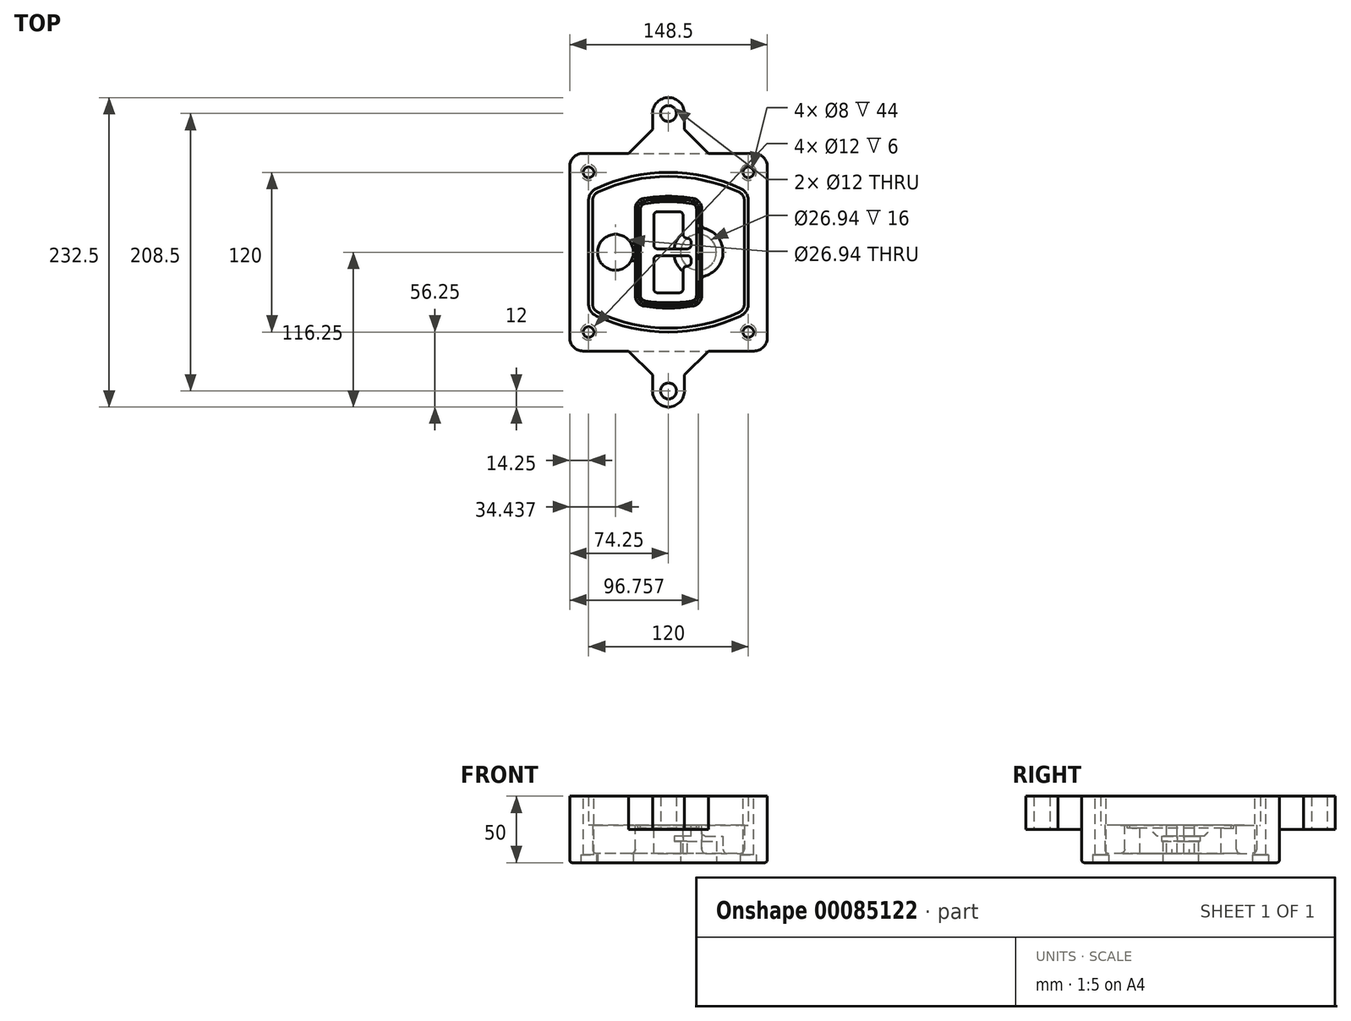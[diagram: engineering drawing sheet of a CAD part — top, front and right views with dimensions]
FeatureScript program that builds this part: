
annotation { "Feature Type Name" : "Feature", "Feature Type Description" : "" }
export const myFeature = defineFeature(function(context is Context, id is Id, definition is map)
    precondition{}
    {
        {
            var Q0;
            Q0=qCreatedBy(makeId("Top.planeOp"),FACE);
            var sketch = newSketch(context, id + "F0", { "sketchPlane" : qUnion([Q0])});
            skPoint(sketch, "E0.rect.middle", {"position": v(0, 0) * mm});
            skLineSegment(sketch, "E1.bottom", {"start": v(-64.25, -74.25) * mm, "end": v(64.25, -74.25) * mm});
            skLineSegment(sketch, "E1.top", {"start": v(-64.25, 74.25) * mm, "end": v(64.25, 74.25) * mm});
            skLineSegment(sketch, "E1.left", {"start": v(-74.25, -64.25) * mm, "end": v(-74.25, 64.25) * mm});
            skLineSegment(sketch, "E1.right", {"start": v(74.25, -64.25) * mm, "end": v(74.25, 64.25) * mm});
            skLineSegment(sketch, "E2", {"start": v(-74.25, 74.25) * mm, "end": v(74.25, -74.25) * mm, "construction": true});
            skLineSegment(sketch, "E3", {"start": v(74.25, 74.25) * mm, "end": v(-74.25, -74.25) * mm, "construction": true});
            skCircle(sketch, "E4", {"center": v(-60, 60) * mm, "radius": 4 * mm});
            skCircle(sketch, "E5", {"center": v(60, 60) * mm, "radius": 4 * mm});
            skCircle(sketch, "E6", {"center": v(60, -60) * mm, "radius": 4 * mm});
            skCircle(sketch, "E7", {"center": v(-60, -60) * mm, "radius": 4 * mm});
            skLineSegment(sketch, "E8", {"start": v(-60, 60) * mm, "end": v(60, 60) * mm, "construction": true});
            skLineSegment(sketch, "E9", {"start": v(60, 60) * mm, "end": v(60, -60) * mm, "construction": true});
            skLineSegment(sketch, "E10", {"start": v(60, -60) * mm, "end": v(-60, -60) * mm, "construction": true});
            skLineSegment(sketch, "E11", {"start": v(-60, -60) * mm, "end": v(-60, 60) * mm, "construction": true});
            skLineSegment(sketch, "E12", {"start": v(-60, 38.83) * mm, "end": v(-60, -38.83) * mm});
            skLineSegment(sketch, "E13", {"start": v(60, 38.83) * mm, "end": v(60, -38.83) * mm});
            skArc(sketch, "E14", {"start": v(54.26, 47.88) * mm, "mid": v(0, 60) * mm, "end": v(-54.26, 47.88) * mm});
            skArc(sketch, "E15", {"start": v(-54.26, -47.88) * mm, "mid": v(0, -60) * mm, "end": v(54.26, -47.88) * mm});
            skLineSegment(sketch, "E16", {"start": v(-60, 0) * mm, "end": v(60, 0) * mm, "construction": true});
            skPoint(sketch, "E17.visualSharp", {"position": v(-60, -45) * mm});
            skArc(sketch, "E17.filletArc", {"start": v(-60, -38.83) * mm, "mid": v(-58.44, -44.2) * mm, "end": v(-54.26, -47.88) * mm});
            skPoint(sketch, "E18.visualSharp", {"position": v(-60, 45) * mm});
            skArc(sketch, "E18.filletArc", {"start": v(-54.26, 47.88) * mm, "mid": v(-58.44, 44.2) * mm, "end": v(-60, 38.83) * mm});
            skPoint(sketch, "E19.visualSharp", {"position": v(60, 45) * mm});
            skArc(sketch, "E19.filletArc", {"start": v(60, 38.83) * mm, "mid": v(58.44, 44.2) * mm, "end": v(54.26, 47.88) * mm});
            skPoint(sketch, "E20.visualSharp", {"position": v(60, -45) * mm});
            skArc(sketch, "E20.filletArc", {"start": v(54.26, -47.88) * mm, "mid": v(58.44, -44.2) * mm, "end": v(60, -38.83) * mm});
            skPoint(sketch, "E21.visualSharp", {"position": v(-74.25, 74.25) * mm});
            skArc(sketch, "E21.filletArc", {"start": v(-64.25, 74.25) * mm, "mid": v(-71.32, 71.32) * mm, "end": v(-74.25, 64.25) * mm});
            skPoint(sketch, "E22.visualSharp", {"position": v(74.25, 74.25) * mm});
            skArc(sketch, "E22.filletArc", {"start": v(74.25, 64.25) * mm, "mid": v(71.32, 71.32) * mm, "end": v(64.25, 74.25) * mm});
            skPoint(sketch, "E23.visualSharp", {"position": v(74.25, -74.25) * mm});
            skArc(sketch, "E23.filletArc", {"start": v(64.25, -74.25) * mm, "mid": v(71.32, -71.32) * mm, "end": v(74.25, -64.25) * mm});
            skPoint(sketch, "E24.visualSharp", {"position": v(-74.25, -74.25) * mm});
            skArc(sketch, "E24.filletArc", {"start": v(-74.25, -64.25) * mm, "mid": v(-71.32, -71.32) * mm, "end": v(-64.25, -74.25) * mm});
            skArc(sketch, "E25.0", {"start": v(57, 38.83) * mm, "mid": v(55.9, 42.58) * mm, "end": v(52.98, 45.17) * mm});
            skLineSegment(sketch, "E25.1", {"start": v(57, 38.83) * mm, "end": v(57, -38.83) * mm});
            skArc(sketch, "E25.2", {"start": v(52.98, -45.17) * mm, "mid": v(55.9, -42.58) * mm, "end": v(57, -38.83) * mm});
            skArc(sketch, "E25.3", {"start": v(-52.98, -45.17) * mm, "mid": v(0, -57) * mm, "end": v(52.98, -45.17) * mm});
            skArc(sketch, "E25.4", {"start": v(-57, -38.83) * mm, "mid": v(-55.9, -42.58) * mm, "end": v(-52.98, -45.17) * mm});
            skArc(sketch, "E25.5", {"start": v(52.98, 45.17) * mm, "mid": v(0, 57) * mm, "end": v(-52.98, 45.17) * mm});
            skLineSegment(sketch, "E25.6", {"start": v(-57, 38.83) * mm, "end": v(-57, -38.83) * mm});
            skArc(sketch, "E25.7", {"start": v(-52.98, 45.17) * mm, "mid": v(-55.9, 42.58) * mm, "end": v(-57, 38.83) * mm});
            skArc(sketch, "E26.0", {"start": v(-55.96, 51.5) * mm, "mid": v(-61.82, 46.33) * mm, "end": v(-64, 38.83) * mm});
            skArc(sketch, "E26.1", {"start": v(55.96, 51.5) * mm, "mid": v(0, 64) * mm, "end": v(-55.96, 51.5) * mm});
            skArc(sketch, "E26.2", {"start": v(64, 38.83) * mm, "mid": v(61.82, 46.33) * mm, "end": v(55.96, 51.5) * mm});
            skLineSegment(sketch, "E26.3", {"start": v(64, 38.83) * mm, "end": v(64, -38.83) * mm});
            skArc(sketch, "E26.4", {"start": v(55.96, -51.5) * mm, "mid": v(61.82, -46.33) * mm, "end": v(64, -38.83) * mm});
            skLineSegment(sketch, "E26.5", {"start": v(-64, 38.83) * mm, "end": v(-64, -38.83) * mm});
            skArc(sketch, "E26.6", {"start": v(-55.96, -51.5) * mm, "mid": v(0, -64) * mm, "end": v(55.96, -51.5) * mm});
            skArc(sketch, "E26.7", {"start": v(-64, -38.83) * mm, "mid": v(-61.82, -46.33) * mm, "end": v(-55.96, -51.5) * mm});
            skSolve(sketch);
        }
        {
            var Q0;
            Q0=makeQuery(id+"F0.imprint","IMPRINT",FACE,{"disambiguationData":[TD([[makeQuery(id+"F0.imprint","IMPRINT",EDGE,{"derivedFrom":sQuery(id+"F0.wireOp",EDGE,"E1.bottom")}),1.0]])]});
            var Q1;
            Q1=makeQuery(id+"F0.imprint","IMPRINT",FACE,{"disambiguationData":[TD([[makeQuery(id+"F0.imprint","IMPRINT",EDGE,{"derivedFrom":sQuery(id+"F0.wireOp",EDGE,"E12")}),1.0]])]});
            var Q2;
            Q2=makeQuery(id+"F0.imprint","IMPRINT",FACE,{"disambiguationData":[TD([[makeQuery(id+"F0.imprint","IMPRINT",EDGE,{"derivedFrom":sQuery(id+"F0.wireOp",EDGE,"E25.0")}),1.0]])]});
            var Q3;
            Q3=makeQuery(id+"F0.imprint","IMPRINT",FACE,{"disambiguationData":[TD([[makeQuery(id+"F0.imprint","IMPRINT",EDGE,{"derivedFrom":sQuery(id+"F0.wireOp",EDGE,"E12")}),-1.0]])]});
            extrude(context, id + "F1", {"entities" : qUnion([Q0, Q1, Q2, Q3]), "oppositeDirection" : true, "depth" : 25 * mm});
        }
        {
            var Q0;
            Q0=makeQuery(id+"F0.imprint","IMPRINT",FACE,{"disambiguationData":[TD([[makeQuery(id+"F0.imprint","IMPRINT",EDGE,{"derivedFrom":sQuery(id+"F0.wireOp",EDGE,"E12")}),1.0]])]});
            extrude(context, id + "F2", {"entities" : qUnion([Q0]), "operationType" : NewBodyOperationType.ADD, "depth" : 3 * mm});
        }
        {
            var Q0;
            Q0=makeQuery(id+"F0.imprint","IMPRINT",FACE,{"disambiguationData":[TD([[makeQuery(id+"F0.imprint","IMPRINT",EDGE,{"derivedFrom":sQuery(id+"F0.wireOp",EDGE,"E25.0")}),1.0]])]});
            extrude(context, id + "F3", {"entities" : qUnion([Q0]), "operationType" : NewBodyOperationType.REMOVE, "oppositeDirection" : true, "depth" : 18 * mm});
        }
        {
            var Q0;
            Q0=makeQuery(id+"F2.opExtrude","CAP_FACE",FACE,{"disambiguationData":[OSD([sQuery(id+"F0.wireOp",EDGE,"E12"),sQuery(id+"F0.wireOp",EDGE,"E13"),sQuery(id+"F0.wireOp",EDGE,"E14"),sQuery(id+"F0.wireOp",EDGE,"E15"),sQuery(id+"F0.wireOp",EDGE,"E17.filletArc"),sQuery(id+"F0.wireOp",EDGE,"E18.filletArc"),sQuery(id+"F0.wireOp",EDGE,"E19.filletArc"),sQuery(id+"F0.wireOp",EDGE,"E20.filletArc"),sQuery(id+"F0.wireOp",EDGE,"E25.0"),sQuery(id+"F0.wireOp",EDGE,"E25.1"),sQuery(id+"F0.wireOp",EDGE,"E25.2"),sQuery(id+"F0.wireOp",EDGE,"E25.3"),sQuery(id+"F0.wireOp",EDGE,"E25.4"),sQuery(id+"F0.wireOp",EDGE,"E25.5"),sQuery(id+"F0.wireOp",EDGE,"E25.6"),sQuery(id+"F0.wireOp",EDGE,"E25.7")])],"isStart":false});
            var sketch = newSketch(context, id + "F4", { "sketchPlane" : qUnion([Q0])});
            skArc(sketch, "E27.0", {"start": v(-18.34, -40.45) * mm, "mid": v(0, -42) * mm, "end": v(18.34, -40.45) * mm});
            skArc(sketch, "E28.0", {"start": v(18.34, 40.45) * mm, "mid": v(0, 42) * mm, "end": v(-18.34, 40.45) * mm});
            skLineSegment(sketch, "E29", {"start": v(-25, 32.57) * mm, "end": v(-25, -32.57) * mm});
            skLineSegment(sketch, "E30", {"start": v(25, 32.57) * mm, "end": v(25, -32.57) * mm});
            skLineSegment(sketch, "E31", {"start": v(-25, 39.1) * mm, "end": v(25, 39.1) * mm, "construction": true});
            skLineSegment(sketch, "E32", {"start": v(-25, -39.1) * mm, "end": v(25, -39.1) * mm, "construction": true});
            skPoint(sketch, "E33.visualSharp", {"position": v(-25, 39.1) * mm});
            skArc(sketch, "E33.filletArc", {"start": v(-18.34, 40.45) * mm, "mid": v(-23.11, 37.73) * mm, "end": v(-25, 32.57) * mm});
            skPoint(sketch, "E34.visualSharp", {"position": v(25, 39.1) * mm});
            skArc(sketch, "E34.filletArc", {"start": v(25, 32.57) * mm, "mid": v(23.11, 37.73) * mm, "end": v(18.34, 40.45) * mm});
            skPoint(sketch, "E35.visualSharp", {"position": v(25, -39.1) * mm});
            skArc(sketch, "E35.filletArc", {"start": v(18.34, -40.45) * mm, "mid": v(23.11, -37.73) * mm, "end": v(25, -32.57) * mm});
            skPoint(sketch, "E36.visualSharp", {"position": v(-25, -39.1) * mm});
            skArc(sketch, "E36.filletArc", {"start": v(-25, -32.57) * mm, "mid": v(-23.11, -37.73) * mm, "end": v(-18.34, -40.45) * mm});
            skArc(sketch, "E37.0", {"start": v(52.98, 45.17) * mm, "mid": v(0, 57) * mm, "end": v(-52.98, 45.17) * mm});
            skArc(sketch, "E37.1", {"start": v(-52.98, 45.17) * mm, "mid": v(-55.9, 42.58) * mm, "end": v(-57, 38.83) * mm});
            skLineSegment(sketch, "E37.2", {"start": v(-57, 38.83) * mm, "end": v(-57, -38.83) * mm});
            skArc(sketch, "E37.3", {"start": v(-57, -38.83) * mm, "mid": v(-55.9, -42.58) * mm, "end": v(-52.98, -45.17) * mm});
            skArc(sketch, "E37.4", {"start": v(-52.98, -45.17) * mm, "mid": v(0, -57) * mm, "end": v(52.98, -45.17) * mm});
            skArc(sketch, "E37.5", {"start": v(52.98, -45.17) * mm, "mid": v(55.9, -42.58) * mm, "end": v(57, -38.83) * mm});
            skLineSegment(sketch, "E37.6", {"start": v(57, 38.83) * mm, "end": v(57, -38.83) * mm});
            skArc(sketch, "E37.7", {"start": v(57, 38.83) * mm, "mid": v(55.9, 42.58) * mm, "end": v(52.98, 45.17) * mm});
            skLineSegment(sketch, "E38.0", {"start": v(23, 32.57) * mm, "end": v(23, -32.57) * mm});
            skArc(sketch, "E38.1", {"start": v(18, -38.48) * mm, "mid": v(21.58, -36.44) * mm, "end": v(23, -32.57) * mm});
            skArc(sketch, "E38.2", {"start": v(-18, -38.48) * mm, "mid": v(0, -40) * mm, "end": v(18, -38.48) * mm});
            skArc(sketch, "E38.3", {"start": v(-23, -32.57) * mm, "mid": v(-21.58, -36.44) * mm, "end": v(-18, -38.48) * mm});
            skLineSegment(sketch, "E38.4", {"start": v(-23, 32.57) * mm, "end": v(-23, -32.57) * mm});
            skArc(sketch, "E38.5", {"start": v(23, 32.57) * mm, "mid": v(21.58, 36.44) * mm, "end": v(18, 38.48) * mm});
            skArc(sketch, "E38.6", {"start": v(-18, 38.48) * mm, "mid": v(-21.58, 36.44) * mm, "end": v(-23, 32.57) * mm});
            skArc(sketch, "E38.7", {"start": v(18, 38.48) * mm, "mid": v(0, 40) * mm, "end": v(-18, 38.48) * mm});
            skArc(sketch, "E39.0", {"start": v(21, 32.57) * mm, "mid": v(20.06, 35.15) * mm, "end": v(17.67, 36.5) * mm});
            skLineSegment(sketch, "E39.1", {"start": v(21, 32.57) * mm, "end": v(21, -32.57) * mm});
            skArc(sketch, "E39.2", {"start": v(17.67, -36.5) * mm, "mid": v(20.06, -35.15) * mm, "end": v(21, -32.57) * mm});
            skArc(sketch, "E39.3", {"start": v(-17.67, -36.5) * mm, "mid": v(0, -38) * mm, "end": v(17.67, -36.5) * mm});
            skArc(sketch, "E39.4", {"start": v(-21, -32.57) * mm, "mid": v(-20.06, -35.15) * mm, "end": v(-17.67, -36.5) * mm});
            skArc(sketch, "E39.5", {"start": v(17.67, 36.5) * mm, "mid": v(0, 38) * mm, "end": v(-17.67, 36.5) * mm});
            skLineSegment(sketch, "E39.6", {"start": v(-21, 32.57) * mm, "end": v(-21, -32.57) * mm});
            skArc(sketch, "E39.7", {"start": v(-17.67, 36.5) * mm, "mid": v(-20.06, 35.15) * mm, "end": v(-21, 32.57) * mm});
            skLineSegment(sketch, "E40", {"start": v(-25, 0) * mm, "end": v(25, 0) * mm, "construction": true});
            skLineSegment(sketch, "E41", {"start": v(-11, 5.5) * mm, "end": v(-11, 27.5) * mm});
            skLineSegment(sketch, "E42", {"start": v(-8, 30.5) * mm, "end": v(8, 30.5) * mm});
            skLineSegment(sketch, "E43", {"start": v(11, 27.5) * mm, "end": v(11, 13.5) * mm});
            skLineSegment(sketch, "E44", {"start": v(14, 10.5) * mm, "end": v(14, 10.5) * mm});
            skLineSegment(sketch, "E45", {"start": v(17, 7.5) * mm, "end": v(17, 5.5) * mm});
            skLineSegment(sketch, "E46", {"start": v(14, 2.5) * mm, "end": v(-8, 2.5) * mm});
            skPoint(sketch, "E47.visualSharp", {"position": v(-11, 30.5) * mm});
            skArc(sketch, "E47.filletArc", {"start": v(-8, 30.5) * mm, "mid": v(-10.12, 29.62) * mm, "end": v(-11, 27.5) * mm});
            skPoint(sketch, "E48.visualSharp", {"position": v(11, 30.5) * mm});
            skArc(sketch, "E48.filletArc", {"start": v(11, 27.5) * mm, "mid": v(10.12, 29.62) * mm, "end": v(8, 30.5) * mm});
            skPoint(sketch, "E49.visualSharp", {"position": v(11, 10.5) * mm});
            skArc(sketch, "E49.filletArc", {"start": v(11, 13.5) * mm, "mid": v(11.88, 11.38) * mm, "end": v(14, 10.5) * mm});
            skPoint(sketch, "E50.visualSharp", {"position": v(17, 10.5) * mm});
            skArc(sketch, "E50.filletArc", {"start": v(17, 7.5) * mm, "mid": v(16.12, 9.62) * mm, "end": v(14, 10.5) * mm});
            skPoint(sketch, "E51.visualSharp", {"position": v(17, 2.5) * mm});
            skArc(sketch, "E51.filletArc", {"start": v(14, 2.5) * mm, "mid": v(16.12, 3.38) * mm, "end": v(17, 5.5) * mm});
            skPoint(sketch, "E52.visualSharp", {"position": v(-11, 2.5) * mm});
            skArc(sketch, "E52.filletArc", {"start": v(-11, 5.5) * mm, "mid": v(-10.12, 3.38) * mm, "end": v(-8, 2.5) * mm});
            skLineSegment(sketch, "E53.0.MirrorCS", {"start": v(14, -2.5) * mm, "end": v(-8, -2.5) * mm});
            skArc(sketch, "E54.0.MirrorCS", {"start": v(-11, -5.5) * mm, "mid": v(-10.12, -3.38) * mm, "end": v(-8, -2.5) * mm});
            skLineSegment(sketch, "E55.0.MirrorCS", {"start": v(-11, -5.5) * mm, "end": v(-11, -27.5) * mm});
            skArc(sketch, "E56.0.MirrorCS", {"start": v(-8, -30.5) * mm, "mid": v(-10.12, -29.62) * mm, "end": v(-11, -27.5) * mm});
            skLineSegment(sketch, "E57.0.MirrorCS", {"start": v(-8, -30.5) * mm, "end": v(8, -30.5) * mm});
            skArc(sketch, "E58.0.MirrorCS", {"start": v(11, -27.5) * mm, "mid": v(10.12, -29.62) * mm, "end": v(8, -30.5) * mm});
            skLineSegment(sketch, "E59.0.MirrorCS", {"start": v(11, -27.5) * mm, "end": v(11, -13.5) * mm});
            skArc(sketch, "E60.0.MirrorCS", {"start": v(11, -13.5) * mm, "mid": v(11.88, -11.38) * mm, "end": v(14, -10.5) * mm});
            skArc(sketch, "E61.0.MirrorCS", {"start": v(17, -7.5) * mm, "mid": v(16.12, -9.62) * mm, "end": v(14, -10.5) * mm});
            skLineSegment(sketch, "E62.0.MirrorCS", {"start": v(17, -7.5) * mm, "end": v(17, -5.5) * mm});
            skArc(sketch, "E63.0.MirrorCS", {"start": v(14, -2.5) * mm, "mid": v(16.12, -3.38) * mm, "end": v(17, -5.5) * mm});
            skSolve(sketch);
        }
        {
            var Q0;
            Q0=makeQuery(id+"F4.imprint","IMPRINT",FACE,{"disambiguationData":[TD([[makeQuery(id+"F4.imprint","IMPRINT",EDGE,{"derivedFrom":sQuery(id+"F4.wireOp",EDGE,"E27.0")}),1.0]])]});
            var Q1;
            Q1=makeQuery(id+"F4.imprint","IMPRINT",FACE,{"disambiguationData":[TD([[makeQuery(id+"F4.imprint","IMPRINT",EDGE,{"derivedFrom":sQuery(id+"F4.wireOp",EDGE,"E38.0")}),-1.0]])]});
            var Q2;
            Q2=makeQuery(id+"F4.imprint","IMPRINT",FACE,{"disambiguationData":[TD([[makeQuery(id+"F4.imprint","IMPRINT",EDGE,{"derivedFrom":sQuery(id+"F4.wireOp",EDGE,"E39.0")}),1.0]])]});
            extrude(context, id + "F5", {"entities" : qUnion([Q0, Q1, Q2]), "operationType" : NewBodyOperationType.ADD, "endBound" : BoundingType.UP_TO_NEXT, "oppositeDirection" : true, "depth" : 25 * mm});
        }
        {
            var Q0;
            Q0=makeQuery(id+"F4.imprint","IMPRINT",FACE,{"disambiguationData":[TD([[makeQuery(id+"F4.imprint","IMPRINT",EDGE,{"derivedFrom":sQuery(id+"F4.wireOp",EDGE,"E38.0")}),-1.0]])]});
            extrude(context, id + "F6", {"entities" : qUnion([Q0]), "operationType" : NewBodyOperationType.REMOVE, "oppositeDirection" : true, "depth" : 2 * mm});
        }
        {
            var Q0;
            Q0=makeQuery(id+"F1.opExtrude","CAP_FACE",FACE,{"disambiguationData":[OSD([sQuery(id+"F0.wireOp",EDGE,"E1.bottom"),sQuery(id+"F0.wireOp",EDGE,"E1.top"),sQuery(id+"F0.wireOp",EDGE,"E1.left"),sQuery(id+"F0.wireOp",EDGE,"E1.right"),sQuery(id+"F0.wireOp",EDGE,"E4"),sQuery(id+"F0.wireOp",EDGE,"E5"),sQuery(id+"F0.wireOp",EDGE,"E6"),sQuery(id+"F0.wireOp",EDGE,"E7"),sQuery(id+"F0.wireOp",EDGE,"E21.filletArc"),sQuery(id+"F0.wireOp",EDGE,"E22.filletArc"),sQuery(id+"F0.wireOp",EDGE,"E23.filletArc"),sQuery(id+"F0.wireOp",EDGE,"E24.filletArc")])],"isStart":false});
            var sketch = newSketch(context, id + "F7", { "sketchPlane" : qUnion([Q0])});
            skCircle(sketch, "E64", {"center": v(22.5, 0) * mm, "radius": 13.47 * mm});
            skCircle(sketch, "E65", {"center": v(-39.81, 0) * mm, "radius": 13.47 * mm});
            skLineSegment(sketch, "E66", {"start": v(74.25, 0) * mm, "end": v(-74.25, 0) * mm});
            skCircle(sketch, "E67", {"center": v(22.5, 0) * mm, "radius": 18.47 * mm});
            skCircle(sketch, "E68", {"center": v(60, -60) * mm, "radius": 6 * mm});
            skCircle(sketch, "E69", {"center": v(-60, -60) * mm, "radius": 6 * mm});
            skCircle(sketch, "E70", {"center": v(-60, 60) * mm, "radius": 6 * mm});
            skCircle(sketch, "E71", {"center": v(60, 60) * mm, "radius": 6 * mm});
            skSolve(sketch);
        }
        {
            var Q0;
            {var subQ1=sQuery(id+"F7.wireOp",EDGE,"E66");var subQ4=sQuery(id+"F7.wireOp",EDGE,"E64");var subQ6=makeQuery(id+"F7.imprint","INTERSECT",VERTEX,{"disambiguationData":[OD(0.0)],"derivedFrom":[subQ4,subQ1]});Q0=makeQuery(id+"F7.imprint","IMPRINT",FACE,{"disambiguationData":[TD([[makeQuery(id+"F7.imprint","IMPRINT",EDGE,{"disambiguationData":[TD([[subQ6,-1.0]])],"derivedFrom":subQ4}),-1.0]])]});}
            var Q1;
            {var subQ0=sQuery(id+"F7.wireOp",EDGE,"E66");var subQ1=sQuery(id+"F7.wireOp",EDGE,"E64");var subQ3=makeQuery(id+"F7.imprint","INTERSECT",VERTEX,{"disambiguationData":[OD(0.0)],"derivedFrom":[subQ1,subQ0]});Q1=makeQuery(id+"F7.imprint","IMPRINT",FACE,{"disambiguationData":[TD([[makeQuery(id+"F7.imprint","IMPRINT",EDGE,{"disambiguationData":[TD([[subQ3,-1.0]])],"derivedFrom":subQ1}),1.0]])]});}
            var Q2;
            {var subQ0=sQuery(id+"F7.wireOp",EDGE,"E66");var subQ1=sQuery(id+"F7.wireOp",EDGE,"E64");var subQ3=makeQuery(id+"F7.imprint","INTERSECT",VERTEX,{"disambiguationData":[OD(0.0)],"derivedFrom":[subQ1,subQ0]});Q2=makeQuery(id+"F7.imprint","IMPRINT",FACE,{"disambiguationData":[TD([[makeQuery(id+"F7.imprint","IMPRINT",EDGE,{"disambiguationData":[TD([[subQ3,1.0]])],"derivedFrom":subQ1}),1.0]])]});}
            var Q3;
            {var subQ1=sQuery(id+"F7.wireOp",EDGE,"E66");var subQ4=sQuery(id+"F7.wireOp",EDGE,"E64");var subQ6=makeQuery(id+"F7.imprint","INTERSECT",VERTEX,{"disambiguationData":[OD(0.0)],"derivedFrom":[subQ4,subQ1]});Q3=makeQuery(id+"F7.imprint","IMPRINT",FACE,{"disambiguationData":[TD([[makeQuery(id+"F7.imprint","IMPRINT",EDGE,{"disambiguationData":[TD([[subQ6,1.0]])],"derivedFrom":subQ4}),-1.0]])]});}
            extrude(context, id + "F8", {"entities" : qUnion([Q0, Q1, Q2, Q3]), "operationType" : NewBodyOperationType.ADD, "oppositeDirection" : true, "depth" : 20 * mm});
        }
        {
            var Q0;
            {var subQ0=sQuery(id+"F7.wireOp",EDGE,"E66");var subQ1=sQuery(id+"F7.wireOp",EDGE,"E64");var subQ3=makeQuery(id+"F7.imprint","INTERSECT",VERTEX,{"disambiguationData":[OD(0.0)],"derivedFrom":[subQ1,subQ0]});Q0=makeQuery(id+"F7.imprint","IMPRINT",FACE,{"disambiguationData":[TD([[makeQuery(id+"F7.imprint","IMPRINT",EDGE,{"disambiguationData":[TD([[subQ3,-1.0]])],"derivedFrom":subQ1}),1.0]])]});}
            var Q1;
            {var subQ0=sQuery(id+"F7.wireOp",EDGE,"E66");var subQ1=sQuery(id+"F7.wireOp",EDGE,"E64");var subQ3=makeQuery(id+"F7.imprint","INTERSECT",VERTEX,{"disambiguationData":[OD(0.0)],"derivedFrom":[subQ1,subQ0]});Q1=makeQuery(id+"F7.imprint","IMPRINT",FACE,{"disambiguationData":[TD([[makeQuery(id+"F7.imprint","IMPRINT",EDGE,{"disambiguationData":[TD([[subQ3,1.0]])],"derivedFrom":subQ1}),1.0]])]});}
            extrude(context, id + "F9", {"entities" : qUnion([Q0, Q1]), "operationType" : NewBodyOperationType.REMOVE, "oppositeDirection" : true, "depth" : 16 * mm});
        }
        {
            var Q0;
            {var subQ0=sQuery(id+"F7.wireOp",EDGE,"E66");var subQ1=sQuery(id+"F7.wireOp",EDGE,"E65");var subQ3=makeQuery(id+"F7.imprint","INTERSECT",VERTEX,{"disambiguationData":[OD(0.0)],"derivedFrom":[subQ1,subQ0]});Q0=makeQuery(id+"F7.imprint","IMPRINT",FACE,{"disambiguationData":[TD([[makeQuery(id+"F7.imprint","IMPRINT",EDGE,{"disambiguationData":[TD([[subQ3,-1.0]])],"derivedFrom":subQ1}),1.0]])]});}
            var Q1;
            {var subQ0=sQuery(id+"F7.wireOp",EDGE,"E66");var subQ1=sQuery(id+"F7.wireOp",EDGE,"E65");var subQ3=makeQuery(id+"F7.imprint","INTERSECT",VERTEX,{"disambiguationData":[OD(0.0)],"derivedFrom":[subQ1,subQ0]});Q1=makeQuery(id+"F7.imprint","IMPRINT",FACE,{"disambiguationData":[TD([[makeQuery(id+"F7.imprint","IMPRINT",EDGE,{"disambiguationData":[TD([[subQ3,1.0]])],"derivedFrom":subQ1}),1.0]])]});}
            extrude(context, id + "F10", {"entities" : qUnion([Q0, Q1]), "operationType" : NewBodyOperationType.REMOVE, "oppositeDirection" : true, "depth" : 25 * mm});
        }
        {
            var Q0;
            Q0=makeQuery(id+"F7.imprint","IMPRINT",FACE,{"disambiguationData":[TD([[makeQuery(id+"F7.imprint","IMPRINT",EDGE,{"derivedFrom":sQuery(id+"F7.wireOp",EDGE,"E68")}),1.0]])]});
            var Q1;
            Q1=makeQuery(id+"F7.imprint","IMPRINT",FACE,{"disambiguationData":[TD([[makeQuery(id+"F7.imprint","IMPRINT",EDGE,{"derivedFrom":makeQuery(id+"F1.opExtrude","CAP_EDGE",EDGE,{"disambiguationData":[OSD([sQuery(id+"F0.wireOp",EDGE,"E5")])],"isStart":false})}),-1.0]])]});
            var Q2;
            Q2=makeQuery(id+"F7.imprint","IMPRINT",FACE,{"disambiguationData":[TD([[makeQuery(id+"F7.imprint","IMPRINT",EDGE,{"derivedFrom":sQuery(id+"F7.wireOp",EDGE,"E69")}),1.0]])]});
            var Q3;
            Q3=makeQuery(id+"F7.imprint","IMPRINT",FACE,{"disambiguationData":[TD([[makeQuery(id+"F7.imprint","IMPRINT",EDGE,{"derivedFrom":makeQuery(id+"F1.opExtrude","CAP_EDGE",EDGE,{"disambiguationData":[OSD([sQuery(id+"F0.wireOp",EDGE,"E4")])],"isStart":false})}),-1.0]])]});
            var Q4;
            Q4=makeQuery(id+"F7.imprint","IMPRINT",FACE,{"disambiguationData":[TD([[makeQuery(id+"F7.imprint","IMPRINT",EDGE,{"derivedFrom":sQuery(id+"F7.wireOp",EDGE,"E70")}),1.0]])]});
            var Q5;
            Q5=makeQuery(id+"F7.imprint","IMPRINT",FACE,{"disambiguationData":[TD([[makeQuery(id+"F7.imprint","IMPRINT",EDGE,{"derivedFrom":makeQuery(id+"F1.opExtrude","CAP_EDGE",EDGE,{"disambiguationData":[OSD([sQuery(id+"F0.wireOp",EDGE,"E7")])],"isStart":false})}),-1.0]])]});
            var Q6;
            Q6=makeQuery(id+"F7.imprint","IMPRINT",FACE,{"disambiguationData":[TD([[makeQuery(id+"F7.imprint","IMPRINT",EDGE,{"derivedFrom":sQuery(id+"F7.wireOp",EDGE,"E71")}),1.0]])]});
            var Q7;
            Q7=makeQuery(id+"F7.imprint","IMPRINT",FACE,{"disambiguationData":[TD([[makeQuery(id+"F7.imprint","IMPRINT",EDGE,{"derivedFrom":makeQuery(id+"F1.opExtrude","CAP_EDGE",EDGE,{"disambiguationData":[OSD([sQuery(id+"F0.wireOp",EDGE,"E6")])],"isStart":false})}),-1.0]])]});
            extrude(context, id + "F11", {"entities" : qUnion([Q0, Q1, Q2, Q3, Q4, Q5, Q6, Q7]), "operationType" : NewBodyOperationType.REMOVE, "oppositeDirection" : true, "depth" : 6 * mm});
        }
        {
            var Q0;
            Q0=makeQuery(id+"F9.boolean.opBoolean","COPY",FACE,{"derivedFrom":makeQuery(id+"F9.opExtrude","CAP_FACE",FACE,{"disambiguationData":[OSD([sQuery(id+"F7.wireOp",EDGE,"E64")])],"isStart":false})});
            var sketch = newSketch(context, id + "F12", { "sketchPlane" : qUnion([Q0])});
            skArc(sketch, "E72.0", {"start": v(11, 14.45) * mm, "mid": v(6.45, 9.13) * mm, "end": v(4.2, 2.5) * mm});
            skArc(sketch, "E72.1", {"start": v(4.2, -2.5) * mm, "mid": v(6.45, -9.13) * mm, "end": v(11, -14.45) * mm});
            skLineSegment(sketch, "E73", {"start": v(4.2, -2.5) * mm, "end": v(14, -2.5) * mm});
            skLineSegment(sketch, "E74.0", {"start": v(14, 2.5) * mm, "end": v(4.2, 2.5) * mm});
            skArc(sketch, "E74.1", {"start": v(14, 2.5) * mm, "mid": v(16.12, 3.38) * mm, "end": v(17, 5.5) * mm});
            skLineSegment(sketch, "E74.2", {"start": v(17, 7.5) * mm, "end": v(17, 5.5) * mm});
            skArc(sketch, "E74.3", {"start": v(17, 7.5) * mm, "mid": v(16.12, 9.62) * mm, "end": v(14, 10.5) * mm});
            skArc(sketch, "E74.4", {"start": v(11, 13.5) * mm, "mid": v(11.88, 11.38) * mm, "end": v(14, 10.5) * mm});
            skLineSegment(sketch, "E74.5", {"start": v(11, 14.45) * mm, "end": v(11, 13.5) * mm});
            skLineSegment(sketch, "E74.7", {"start": v(14, -2.5) * mm, "end": v(4.2, -2.5) * mm});
            skArc(sketch, "E74.8", {"start": v(14, -2.5) * mm, "mid": v(16.12, -3.38) * mm, "end": v(17, -5.5) * mm});
            skLineSegment(sketch, "E74.9", {"start": v(17, -7.5) * mm, "end": v(17, -5.5) * mm});
            skArc(sketch, "E74.10", {"start": v(17, -7.5) * mm, "mid": v(16.12, -9.62) * mm, "end": v(14, -10.5) * mm});
            skArc(sketch, "E74.11", {"start": v(11, -13.5) * mm, "mid": v(11.88, -11.38) * mm, "end": v(14, -10.5) * mm});
            skLineSegment(sketch, "E74.12", {"start": v(11, -14.45) * mm, "end": v(11, -13.5) * mm});
            skPoint(sketch, "E75.orphan", {"position": v(11, -27.5) * mm});
            skPoint(sketch, "E76.orphan", {"position": v(-8, -2.5) * mm});
            skPoint(sketch, "E77.orphan", {"position": v(-8, 2.5) * mm});
            skPoint(sketch, "E78.orphan", {"position": v(11, 27.5) * mm});
            skSolve(sketch);
        }
        {
            var Q0;
            {var subQ7=sQuery(id+"F12.wireOp",EDGE,"E72.0");var subQ14=sQuery(id+"F12.wireOp",EDGE,"E72.1");var subQ16=sQuery(id+"F12.wireOp",EDGE,"E74.1");var subQ18=sQuery(id+"F12.wireOp",EDGE,"E74.8");Q0=qUnion([makeQuery(id+"F12.imprint","IMPRINT",FACE,{"disambiguationData":[TD([[makeQuery(id+"F12.imprint","IMPRINT",EDGE,{"derivedFrom":subQ7}),1.0]])]}),makeQuery(id+"F12.imprint","IMPRINT",FACE,{"disambiguationData":[TD([[makeQuery(id+"F12.imprint","IMPRINT",EDGE,{"derivedFrom":subQ14}),1.0]])]}),makeQuery(id+"F12.imprint","IMPRINT",FACE,{"disambiguationData":[TD([[makeQuery(id+"F12.imprint","IMPRINT",EDGE,{"derivedFrom":subQ16}),1.0]])]}),makeQuery(id+"F12.imprint","IMPRINT",FACE,{"disambiguationData":[TD([[makeQuery(id+"F12.imprint","IMPRINT",EDGE,{"derivedFrom":subQ18}),-1.0]])]})]);}
            var Q1;
            Q1=makeQuery(id+"F5.boolean.opBoolean","SPLIT",FACE,{"disambiguationData":[TD([makeQuery(id+"F5.opExtrude","SWEPT_FACE",FACE,{"disambiguationData":[OSD([sQuery(id+"F4.wireOp",EDGE,"E41")])]})])],"derivedFrom":makeQuery(id+"F3.boolean.opBoolean","COPY",FACE,{"derivedFrom":makeQuery(id+"F3.opExtrude","CAP_FACE",FACE,{"disambiguationData":[OSD([sQuery(id+"F0.wireOp",EDGE,"E25.0"),sQuery(id+"F0.wireOp",EDGE,"E25.1"),sQuery(id+"F0.wireOp",EDGE,"E25.2"),sQuery(id+"F0.wireOp",EDGE,"E25.3"),sQuery(id+"F0.wireOp",EDGE,"E25.4"),sQuery(id+"F0.wireOp",EDGE,"E25.5"),sQuery(id+"F0.wireOp",EDGE,"E25.6"),sQuery(id+"F0.wireOp",EDGE,"E25.7")])],"isStart":false})})});
            extrude(context, id + "F13", {"entities" : qUnion([Q0]), "operationType" : NewBodyOperationType.REMOVE, "endBound" : BoundingType.UP_TO_SURFACE, "endBoundEntityFace" : qUnion([Q1]), "depth" : 25 * mm});
        }
        {
            var Q0;
            Q0=makeQuery(id+"F3.boolean.opBoolean","COPY",EDGE,{"derivedFrom":makeQuery(id+"F3.opExtrude","CAP_EDGE",EDGE,{"disambiguationData":[OSD([sQuery(id+"F0.wireOp",EDGE,"E25.6")])],"isStart":false})});
            var Q1;
            Q1=makeQuery(id+"F8.boolean.opBoolean","INTERSECT",EDGE,{"derivedFrom":[makeQuery(id+"F5.opExtrude","SWEPT_FACE",FACE,{"disambiguationData":[OSD([sQuery(id+"F4.wireOp",EDGE,"E30")])]}),makeQuery(id+"F8.opExtrude","CAP_FACE",FACE,{"disambiguationData":[OSD([sQuery(id+"F7.wireOp",EDGE,"E67")])],"isStart":false})]});
            var Q2;
            Q2=makeQuery(id+"F8.boolean.opBoolean","INTERSECT",EDGE,{"disambiguationData":[OD(1.0)],"derivedFrom":[makeQuery(id+"F5.opExtrude","SWEPT_FACE",FACE,{"disambiguationData":[OSD([sQuery(id+"F4.wireOp",EDGE,"E30")])]}),makeQuery(id+"F8.opExtrude","SWEPT_FACE",FACE,{"disambiguationData":[OSD([sQuery(id+"F7.wireOp",EDGE,"E67")])]})]});
            var Q3;
            {var subQ0=sQuery(id+"F4.wireOp",EDGE,"E30");Q3=makeQuery(id+"F8.boolean.opBoolean","SPLIT",EDGE,{"disambiguationData":[TD([makeQuery(id+"F5.opExtrude","SWEPT_FACE",FACE,{"disambiguationData":[OSD([sQuery(id+"F4.wireOp",EDGE,"E35.filletArc")])]})])],"derivedFrom":makeQuery(id+"F5.opExtrude","CAP_EDGE",EDGE,{"disambiguationData":[OSD([subQ0])],"isStart":false})});}
            var Q4;
            {var subQ0=sQuery(id+"F0.wireOp",EDGE,"E25.7");var subQ1=sQuery(id+"F0.wireOp",EDGE,"E25.1");var subQ2=sQuery(id+"F0.wireOp",EDGE,"E25.6");var subQ3=sQuery(id+"F0.wireOp",EDGE,"E25.5");var subQ4=sQuery(id+"F0.wireOp",EDGE,"E25.4");var subQ5=sQuery(id+"F0.wireOp",EDGE,"E25.0");var subQ6=sQuery(id+"F0.wireOp",EDGE,"E25.2");var subQ7=sQuery(id+"F0.wireOp",EDGE,"E25.3");Q4=makeQuery(id+"F8.boolean.opBoolean","INTERSECT",EDGE,{"derivedFrom":[makeQuery(id+"F5.boolean.opBoolean","SPLIT",FACE,{"disambiguationData":[TD([makeQuery(id+"F2.opExtrude","SWEPT_FACE",FACE,{"disambiguationData":[OSD([subQ5])]})])],"derivedFrom":makeQuery(id+"F3.boolean.opBoolean","COPY",FACE,{"derivedFrom":makeQuery(id+"F3.opExtrude","CAP_FACE",FACE,{"disambiguationData":[OSD([subQ5,subQ1,subQ6,subQ7,subQ4,subQ3,subQ2,subQ0])],"isStart":false})})}),makeQuery(id+"F8.opExtrude","SWEPT_FACE",FACE,{"disambiguationData":[OSD([sQuery(id+"F7.wireOp",EDGE,"E67")])]})]});}
            var Q5;
            Q5=makeQuery(id+"F8.boolean.opBoolean","INTERSECT",EDGE,{"disambiguationData":[OD(0.0)],"derivedFrom":[makeQuery(id+"F5.opExtrude","SWEPT_FACE",FACE,{"disambiguationData":[OSD([sQuery(id+"F4.wireOp",EDGE,"E30")])]}),makeQuery(id+"F8.opExtrude","SWEPT_FACE",FACE,{"disambiguationData":[OSD([sQuery(id+"F7.wireOp",EDGE,"E67")])]})]});
            fillet(context, id + "F14", {"entities" : qUnion([Q0, Q1, Q2, Q3, Q4, Q5]), "radius" : 3 * mm, "tangentPropagation" : true, "allowEdgeOverflow" : false});
        }
        {
            var Q0;
            Q0=makeQuery(id+"F1.opExtrude","CAP_EDGE",EDGE,{"disambiguationData":[OSD([sQuery(id+"F0.wireOp",EDGE,"E1.bottom")])],"isStart":false});
            fillet(context, id + "F15", {"entities" : qUnion([Q0]), "radius" : 2 * mm, "tangentPropagation" : true, "allowEdgeOverflow" : false});
        }
        {
            var Q0;
            {var subQ0=sQuery(id+"F0.wireOp",EDGE,"E22.filletArc");var subQ1=sQuery(id+"F0.wireOp",EDGE,"E7");var subQ2=sQuery(id+"F0.wireOp",EDGE,"E6");var subQ3=sQuery(id+"F0.wireOp",EDGE,"E5");var subQ4=sQuery(id+"F0.wireOp",EDGE,"E4");var subQ5=sQuery(id+"F0.wireOp",EDGE,"E1.bottom");var subQ6=sQuery(id+"F0.wireOp",EDGE,"E21.filletArc");var subQ7=sQuery(id+"F0.wireOp",EDGE,"E1.top");var subQ8=sQuery(id+"F0.wireOp",EDGE,"E1.left");var subQ9=sQuery(id+"F0.wireOp",EDGE,"E1.right");var subQ10=sQuery(id+"F0.wireOp",EDGE,"E23.filletArc");var subQ11=sQuery(id+"F0.wireOp",EDGE,"E24.filletArc");Q0=makeQuery(id+"F2.boolean.opBoolean","SPLIT",FACE,{"disambiguationData":[TD([makeQuery(id+"F1.opExtrude","SWEPT_FACE",FACE,{"disambiguationData":[OSD([subQ5])]})])],"derivedFrom":makeQuery(id+"F1.opExtrude","CAP_FACE",FACE,{"disambiguationData":[OSD([subQ5,subQ7,subQ8,subQ9,subQ4,subQ3,subQ2,subQ1,subQ6,subQ0,subQ10,subQ11])],"isStart":true})});}
            var sketch = newSketch(context, id + "F16", { "sketchPlane" : qUnion([Q0])});
            skLineSegment(sketch, "E79", {"start": v(0, 74.25) * mm, "end": v(0, 104.25) * mm, "construction": true});
            skPoint(sketch, "E79.endSnap0", {"position": v(0, 74.25) * mm});
            skCircle(sketch, "E80", {"center": v(0, 104.25) * mm, "radius": 6 * mm});
            skArc(sketch, "E81", {"start": v(12, 104.25) * mm, "mid": v(0, 116.25) * mm, "end": v(-12, 104.25) * mm});
            skLineSegment(sketch, "E82", {"start": v(12, 104.25) * mm, "end": v(12, 92.25) * mm});
            skLineSegment(sketch, "E83", {"start": v(-12, 104.25) * mm, "end": v(-12, 92.25) * mm});
            skLineSegment(sketch, "E84", {"start": v(12, 92.25) * mm, "end": v(30, 74.25) * mm});
            skLineSegment(sketch, "E85", {"start": v(-12, 92.25) * mm, "end": v(-30, 74.25) * mm});
            skLineSegment(sketch, "E86", {"start": v(-54.47, 74.25) * mm, "end": v(79.4, 74.25) * mm, "construction": true});
            skLineSegment(sketch, "E87", {"start": v(-74.25, 0) * mm, "end": v(74.25, 0) * mm, "construction": true});
            skLineSegment(sketch, "E88.MirrorCS", {"start": v(12, -92.25) * mm, "end": v(30, -74.25) * mm});
            skLineSegment(sketch, "E89.MirrorCS", {"start": v(-12, -92.25) * mm, "end": v(-30, -74.25) * mm});
            skLineSegment(sketch, "E90.MirrorCS", {"start": v(-12, -104.25) * mm, "end": v(-12, -92.25) * mm});
            skLineSegment(sketch, "E91.MirrorCS", {"start": v(12, -104.25) * mm, "end": v(12, -92.25) * mm});
            skLineSegment(sketch, "E92.MirrorCS", {"start": v(0, -74.25) * mm, "end": v(0, -104.25) * mm, "construction": true});
            skCircle(sketch, "E93.MirrorC", {"center": v(0, -104.25) * mm, "radius": 6 * mm});
            skArc(sketch, "E94.MirrorCS", {"start": v(12, -104.25) * mm, "mid": v(0, -116.25) * mm, "end": v(-12, -104.25) * mm});
            skSolve(sketch);
        }
        {
            var Q0;
            Q0=makeQuery(id+"F16.imprint","IMPRINT",FACE,{"disambiguationData":[TD([[makeQuery(id+"F16.imprint","IMPRINT",EDGE,{"derivedFrom":sQuery(id+"F16.wireOp",EDGE,"E80")}),-1.0]])]});
            var Q1;
            Q1=makeQuery(id+"F16.imprint","IMPRINT",FACE,{"disambiguationData":[TD([[makeQuery(id+"F16.imprint","IMPRINT",EDGE,{"derivedFrom":makeQuery(id+"F1.opExtrude","CAP_EDGE",EDGE,{"disambiguationData":[OSD([sQuery(id+"F0.wireOp",EDGE,"E1.left")])],"isStart":true})}),-1.0]])]});
            var Q2;
            {var subQ0=sQuery(id+"F16.wireOp",EDGE,"E88.MirrorCS");Q2=makeQuery(id+"F16.imprint","IMPRINT",FACE,{"disambiguationData":[TD([[makeQuery(id+"F16.imprint","IMPRINT",EDGE,{"derivedFrom":subQ0}),1.0]])]});}
            extrude(context, id + "F17", {"entities" : qUnion([Q0, Q1, Q2]), "operationType" : NewBodyOperationType.ADD, "depth" : 25 * mm});
        }
    });
